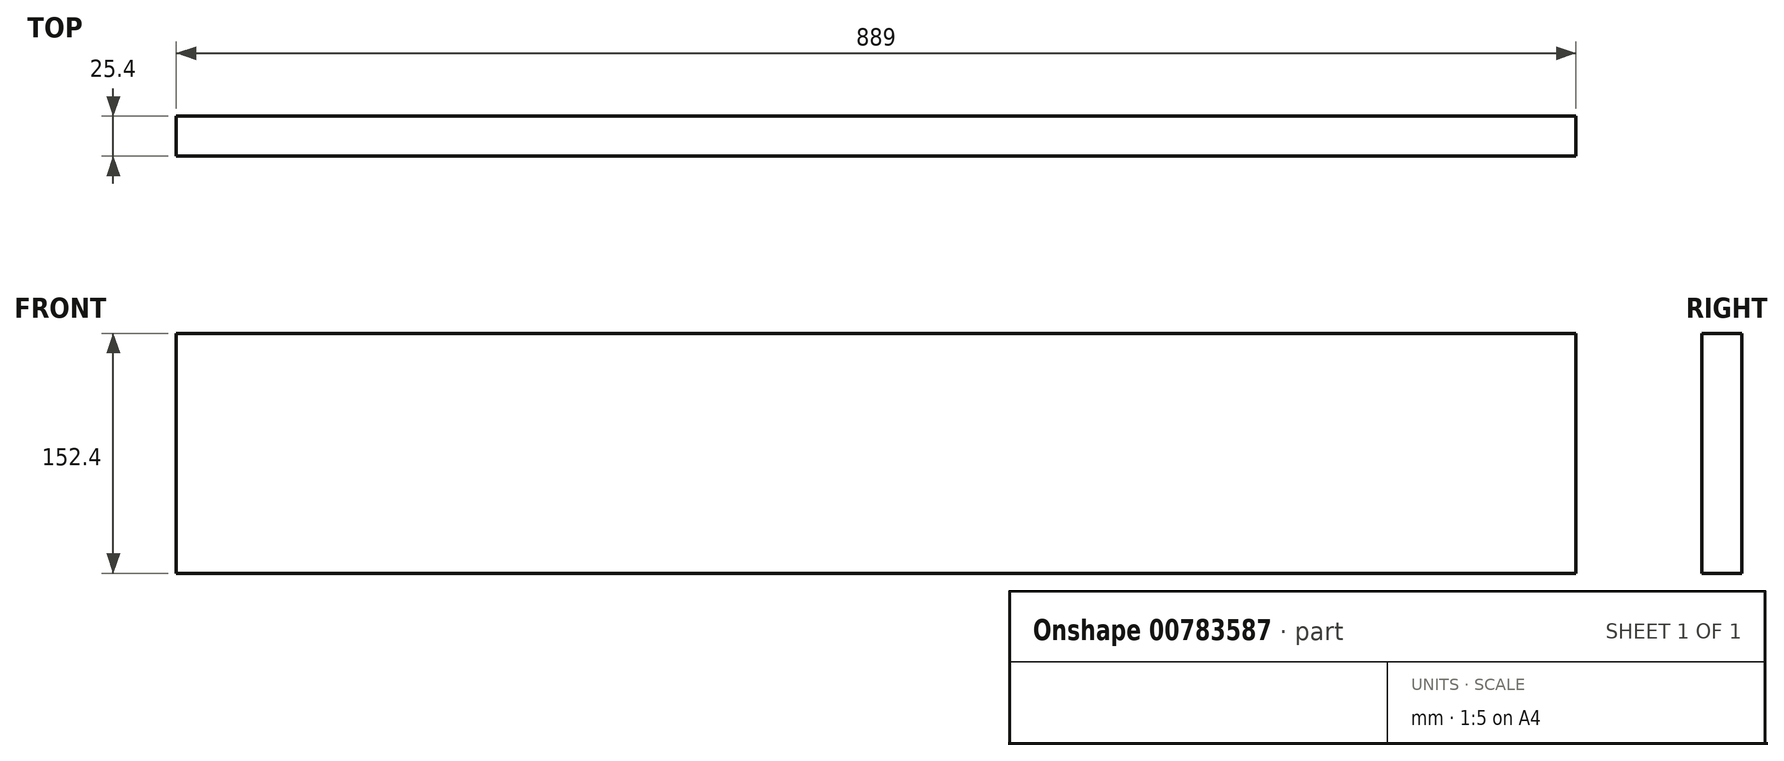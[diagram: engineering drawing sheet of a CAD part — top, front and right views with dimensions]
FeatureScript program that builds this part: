
annotation { "Feature Type Name" : "Feature", "Feature Type Description" : "" }
export const myFeature = defineFeature(function(context is Context, id is Id, definition is map)
    precondition{}
    {
        {
            var Q0;
            Q0=qCreatedBy(makeId("Front.planeOp"),FACE);
            var sketch = newSketch(context, id + "F0", { "sketchPlane" : qUnion([Q0])});
            skLineSegment(sketch, "E0.bottom", {"start": v(0, 0) * mm, "end": v(889, 0) * mm});
            skLineSegment(sketch, "E0.top", {"start": v(0, 152.4) * mm, "end": v(381, 152.4) * mm});
            skLineSegment(sketch, "E0.left", {"start": v(0, 0) * mm, "end": v(0, 152.4) * mm});
            skLineSegment(sketch, "E0.right", {"start": v(889, 0) * mm, "end": v(889, 76.2) * mm});
            skLineSegment(sketch, "E1", {"start": v(381, 152.4) * mm, "end": v(889, 152.4) * mm});
            skLineSegment(sketch, "E2", {"start": v(889, 76.2) * mm, "end": v(889, 152.4) * mm});
            skSolve(sketch);
        }
        {
            var Q0;
            Q0=makeQuery(id+"F0.imprint","IMPRINT",FACE,{"disambiguationData":[TD([[makeQuery(id+"F0.imprint","IMPRINT",EDGE,{"derivedFrom":sQuery(id+"F0.wireOp",EDGE,"E0.bottom")}),1.0]])]});
            extrude(context, id + "F1", {"entities" : qUnion([Q0]), "depth" : 25.4 * mm, "offsetDistance" : 25.4 * mm});
        }
    });
